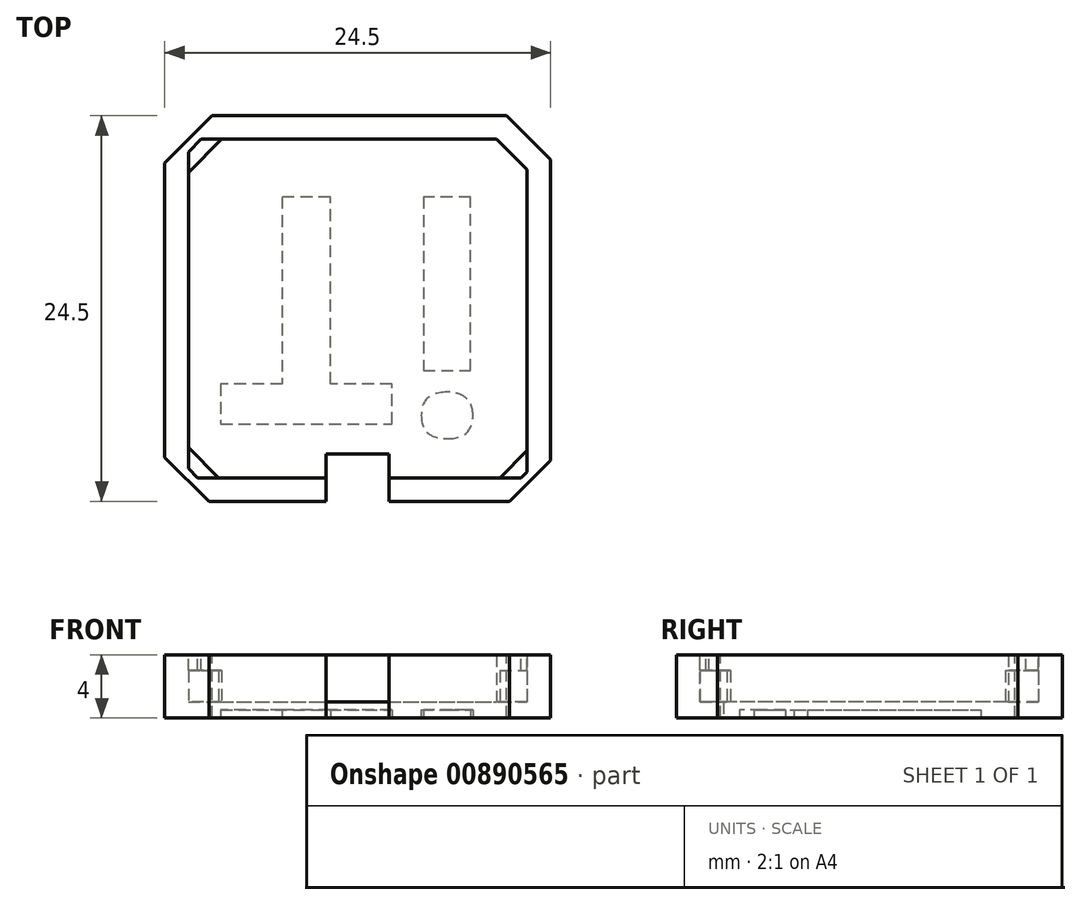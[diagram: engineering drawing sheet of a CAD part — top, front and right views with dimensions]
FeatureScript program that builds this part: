
annotation { "Feature Type Name" : "Feature", "Feature Type Description" : "" }
export const myFeature = defineFeature(function(context is Context, id is Id, definition is map)
    precondition{}
    {
        {
            var Q0;
            Q0=qCreatedBy(makeId("Top.planeOp"),FACE);
            var sketch = newSketch(context, id + "F0", { "sketchPlane" : qUnion([Q0])});
            skLineSegment(sketch, "E0.bottom", {"start": v(-12.25, 12.25) * mm, "end": v(12.25, 12.25) * mm});
            skLineSegment(sketch, "E0.top", {"start": v(-12.25, -12.25) * mm, "end": v(12.25, -12.25) * mm});
            skLineSegment(sketch, "E0.left", {"start": v(-12.25, 12.25) * mm, "end": v(-12.25, -12.25) * mm});
            skLineSegment(sketch, "E0.right", {"start": v(12.25, 12.25) * mm, "end": v(12.25, -12.25) * mm});
            skPoint(sketch, "E0.middle", {"position": v(0, 0) * mm});
            skLineSegment(sketch, "E1", {"start": v(-9.25, 12.25) * mm, "end": v(-12.25, 9.25) * mm});
            skLineSegment(sketch, "E2.1.0", {"start": v(-12.25, -9.45) * mm, "end": v(-9.25, -12.45) * mm});
            skLineSegment(sketch, "E2.2.0", {"start": v(9.45, -12.45) * mm, "end": v(12.45, -9.45) * mm});
            skLineSegment(sketch, "E2.3.0", {"start": v(12.45, 9.25) * mm, "end": v(9.45, 12.25) * mm});
            skPoint(sketch, "E2.center", {"position": v(0.1, -0.1) * mm});
            skSolve(sketch);
        }
        {
            var Q0;
            {var subQ3=sQuery(id+"F0.wireOp",EDGE,"E1");Q0=makeQuery(id+"F0.imprint","IMPRINT",FACE,{"disambiguationData":[TD([[makeQuery(id+"F0.imprint","IMPRINT",EDGE,{"derivedFrom":subQ3}),1.0]])]});}
            extrude(context, id + "F1", {"entities" : qUnion([Q0]), "oppositeDirection" : true, "depth" : 1 * mm, "offsetDistance" : 25 * mm});
        }
        {
            var Q0;
            Q0=makeQuery(id+"F1.opExtrude","CAP_FACE",FACE,{"disambiguationData":[OSD([sQuery(id+"F0.wireOp",EDGE,"E0.bottom"),sQuery(id+"F0.wireOp",EDGE,"E0.top"),sQuery(id+"F0.wireOp",EDGE,"E0.left"),sQuery(id+"F0.wireOp",EDGE,"E0.right"),sQuery(id+"F0.wireOp",EDGE,"E1"),sQuery(id+"F0.wireOp",EDGE,"E2.1.0"),sQuery(id+"F0.wireOp",EDGE,"E2.2.0"),sQuery(id+"F0.wireOp",EDGE,"E2.3.0")])],"isStart":true});
            var sketch = newSketch(context, id + "F2", { "sketchPlane" : qUnion([Q0])});
            skLineSegment(sketch, "E3.0", {"start": v(-8.63, 10.75) * mm, "end": v(8.83, 10.75) * mm});
            skLineSegment(sketch, "E3.1", {"start": v(10.75, 8.83) * mm, "end": v(8.83, 10.75) * mm});
            skLineSegment(sketch, "E3.2", {"start": v(-8.63, 10.75) * mm, "end": v(-10.75, 8.63) * mm});
            skLineSegment(sketch, "E3.3", {"start": v(10.75, 8.83) * mm, "end": v(10.75, -9.03) * mm});
            skLineSegment(sketch, "E3.4", {"start": v(-10.75, 8.63) * mm, "end": v(-10.75, -8.83) * mm});
            skLineSegment(sketch, "E3.5", {"start": v(-10.75, -8.83) * mm, "end": v(-8.83, -10.75) * mm});
            skLineSegment(sketch, "E3.6", {"start": v(-8.83, -10.75) * mm, "end": v(9.03, -10.75) * mm});
            skLineSegment(sketch, "E3.7", {"start": v(9.03, -10.75) * mm, "end": v(10.75, -9.03) * mm});
            skSolve(sketch);
        }
        {
            var Q0;
            Q0=makeQuery(id+"F2.imprint","IMPRINT",FACE,{"disambiguationData":[TD([[makeQuery(id+"F2.imprint","IMPRINT",EDGE,{"derivedFrom":sQuery(id+"F2.wireOp",EDGE,"E3.0")}),1.0]])]});
            extrude(context, id + "F3", {"entities" : qUnion([Q0]), "operationType" : NewBodyOperationType.ADD, "depth" : 3 * mm, "offsetDistance" : 25 * mm});
        }
        {
            var Q0;
            {var subQ0=sQuery(id+"F0.wireOp",EDGE,"E0.top");Q0=makeQuery(id+"F3.boolean.opBoolean","MERGE",FACE,{"derivedFrom":[makeQuery(id+"F1.opExtrude","SWEPT_FACE",FACE,{"disambiguationData":[OSD([subQ0])]}),makeQuery(id+"F3.opExtrude","SWEPT_FACE",FACE,{"disambiguationData":[OSD([subQ0])]})]});}
            var sketch = newSketch(context, id + "F4", { "sketchPlane" : qUnion([Q0])});
            skLineSegment(sketch, "E4.bottom", {"start": v(-1.7, 3) * mm, "end": v(1.7, 3) * mm});
            skLineSegment(sketch, "E4.top", {"start": v(-1.7, 0) * mm, "end": v(1.7, 0) * mm});
            skLineSegment(sketch, "E4.left", {"start": v(-1.7, 3) * mm, "end": v(-1.7, 0) * mm});
            skLineSegment(sketch, "E4.right", {"start": v(1.7, 3) * mm, "end": v(1.7, 0) * mm});
            skSolve(sketch);
        }
        {
            var Q0;
            Q0=makeQuery(id+"F4.imprint","IMPRINT",FACE,{"disambiguationData":[TD([[makeQuery(id+"F4.imprint","IMPRINT",EDGE,{"derivedFrom":sQuery(id+"F4.wireOp",EDGE,"E4.bottom")}),-1.0]])]});
            extrude(context, id + "F5", {"entities" : qUnion([Q0]), "operationType" : NewBodyOperationType.REMOVE, "oppositeDirection" : true, "depth" : 5 * mm, "offsetDistance" : 25 * mm});
        }
        {
            var Q0;
            Q0=makeQuery(id+"F3.opExtrude","CAP_FACE",FACE,{"disambiguationData":[OSD([sQuery(id+"F0.wireOp",EDGE,"E0.bottom"),sQuery(id+"F0.wireOp",EDGE,"E0.top"),sQuery(id+"F0.wireOp",EDGE,"E0.left"),sQuery(id+"F0.wireOp",EDGE,"E0.right"),sQuery(id+"F0.wireOp",EDGE,"E1"),sQuery(id+"F0.wireOp",EDGE,"E2.1.0"),sQuery(id+"F0.wireOp",EDGE,"E2.2.0"),sQuery(id+"F0.wireOp",EDGE,"E2.3.0"),sQuery(id+"F2.wireOp",EDGE,"E3.0"),sQuery(id+"F2.wireOp",EDGE,"E3.1"),sQuery(id+"F2.wireOp",EDGE,"E3.2"),sQuery(id+"F2.wireOp",EDGE,"E3.3"),sQuery(id+"F2.wireOp",EDGE,"E3.4"),sQuery(id+"F2.wireOp",EDGE,"E3.5"),sQuery(id+"F2.wireOp",EDGE,"E3.6"),sQuery(id+"F2.wireOp",EDGE,"E3.7")])],"isStart":false});
            var sketch = newSketch(context, id + "F6", { "sketchPlane" : qUnion([Q0])});
            skLineSegment(sketch, "E5", {"start": v(9.03, -10.75) * mm, "end": v(10.38, -10.75) * mm});
            skLineSegment(sketch, "E6", {"start": v(10.38, -10.75) * mm, "end": v(10.75, -10.38) * mm});
            skLineSegment(sketch, "E7", {"start": v(10.75, -10.38) * mm, "end": v(10.75, -9.03) * mm});
            skLineSegment(sketch, "E8", {"start": v(10.75, -9.03) * mm, "end": v(9.03, -10.75) * mm});
            skLineSegment(sketch, "E9", {"start": v(-8.83, -10.75) * mm, "end": v(-10.16, -10.75) * mm});
            skLineSegment(sketch, "E10", {"start": v(-10.16, -10.75) * mm, "end": v(-10.75, -10.18) * mm});
            skLineSegment(sketch, "E11", {"start": v(-10.75, -10.18) * mm, "end": v(-10.75, -8.83) * mm});
            skLineSegment(sketch, "E12", {"start": v(-10.75, -8.83) * mm, "end": v(-8.83, -10.75) * mm});
            skLineSegment(sketch, "E13", {"start": v(-10.75, 8.63) * mm, "end": v(-10.75, 9.95) * mm});
            skLineSegment(sketch, "E14", {"start": v(-10.75, 9.95) * mm, "end": v(-9.95, 10.75) * mm});
            skLineSegment(sketch, "E15", {"start": v(-9.95, 10.75) * mm, "end": v(-8.63, 10.75) * mm});
            skLineSegment(sketch, "E16", {"start": v(-8.63, 10.75) * mm, "end": v(-10.75, 8.63) * mm});
            skSolve(sketch);
        }
        {
            var Q0;
            Q0=makeQuery(id+"F6.imprint","IMPRINT",FACE,{"disambiguationData":[TD([[makeQuery(id+"F6.imprint","IMPRINT",EDGE,{"derivedFrom":sQuery(id+"F6.wireOp",EDGE,"E5")}),1.0]])]});
            var Q1;
            Q1=makeQuery(id+"F6.imprint","IMPRINT",FACE,{"disambiguationData":[TD([[makeQuery(id+"F6.imprint","IMPRINT",EDGE,{"derivedFrom":sQuery(id+"F6.wireOp",EDGE,"E9")}),-1.0]])]});
            var Q2;
            Q2=makeQuery(id+"F6.imprint","IMPRINT",FACE,{"disambiguationData":[TD([[makeQuery(id+"F6.imprint","IMPRINT",EDGE,{"derivedFrom":sQuery(id+"F6.wireOp",EDGE,"E13")}),-1.0]])]});
            extrude(context, id + "F7", {"entities" : qUnion([Q0, Q1, Q2]), "operationType" : NewBodyOperationType.REMOVE, "oppositeDirection" : true, "depth" : 1 * mm, "offsetDistance" : 25 * mm});
        }
        {
            var Q0;
            Q0=makeQuery(id+"F1.opExtrude","CAP_FACE",FACE,{"disambiguationData":[OSD([sQuery(id+"F0.wireOp",EDGE,"E0.bottom"),sQuery(id+"F0.wireOp",EDGE,"E0.top"),sQuery(id+"F0.wireOp",EDGE,"E0.left"),sQuery(id+"F0.wireOp",EDGE,"E0.right"),sQuery(id+"F0.wireOp",EDGE,"E1"),sQuery(id+"F0.wireOp",EDGE,"E2.1.0"),sQuery(id+"F0.wireOp",EDGE,"E2.2.0"),sQuery(id+"F0.wireOp",EDGE,"E2.3.0")])],"isStart":false});
            var sketch = newSketch(context, id + "F8", { "sketchPlane" : qUnion([Q0])});
            skText(sketch, "E17", { "text": "Ti", "fontName": "OpenSans-Bold.ttf"});
            const initialGuessF8  = {"E17": [-0.00911, -0.00709, 1, 0, 0.01455]};
            skSetInitialGuess(sketch, initialGuessF8);
            skSolve(sketch);
        }
        {
            var Q0;
            Q0 = qSketchRegion(id + "F8", true);
            extrude(context, id + "F9", {"entities" : qUnion([Q0]), "operationType" : NewBodyOperationType.REMOVE, "oppositeDirection" : true, "depth" : 0.5 * mm, "offsetDistance" : 25 * mm});
        }
        {
            var Q0;
            Q0=makeQuery(id+"F1.opExtrude","CAP_FACE",FACE,{"disambiguationData":[OSD([sQuery(id+"F0.wireOp",EDGE,"E0.bottom"),sQuery(id+"F0.wireOp",EDGE,"E0.top"),sQuery(id+"F0.wireOp",EDGE,"E0.left"),sQuery(id+"F0.wireOp",EDGE,"E0.right"),sQuery(id+"F0.wireOp",EDGE,"E1"),sQuery(id+"F0.wireOp",EDGE,"E2.1.0"),sQuery(id+"F0.wireOp",EDGE,"E2.2.0"),sQuery(id+"F0.wireOp",EDGE,"E2.3.0")])],"isStart":false});
            var sketch = newSketch(context, id + "F10", { "sketchPlane" : qUnion([Q0])});
            skLineSegment(sketch, "E18.bottom", {"start": v(-2, 12.25) * mm, "end": v(2, 12.25) * mm});
            skLineSegment(sketch, "E18.top", {"start": v(-2, 9.25) * mm, "end": v(2, 9.25) * mm});
            skLineSegment(sketch, "E18.left", {"start": v(-2, 12.25) * mm, "end": v(-2, 9.25) * mm});
            skLineSegment(sketch, "E18.right", {"start": v(2, 12.25) * mm, "end": v(2, 9.25) * mm});
            skSolve(sketch);
        }
        {
            var Q0;
            Q0=makeQuery(id+"F10.imprint","IMPRINT",FACE,{"disambiguationData":[TD([[makeQuery(id+"F10.imprint","IMPRINT",EDGE,{"derivedFrom":sQuery(id+"F10.wireOp",EDGE,"E18.bottom")}),-1.0]])]});
            extrude(context, id + "F11", {"entities" : qUnion([Q0]), "operationType" : NewBodyOperationType.REMOVE, "oppositeDirection" : true, "depth" : 5 * mm, "offsetDistance" : 25 * mm});
        }
    });
